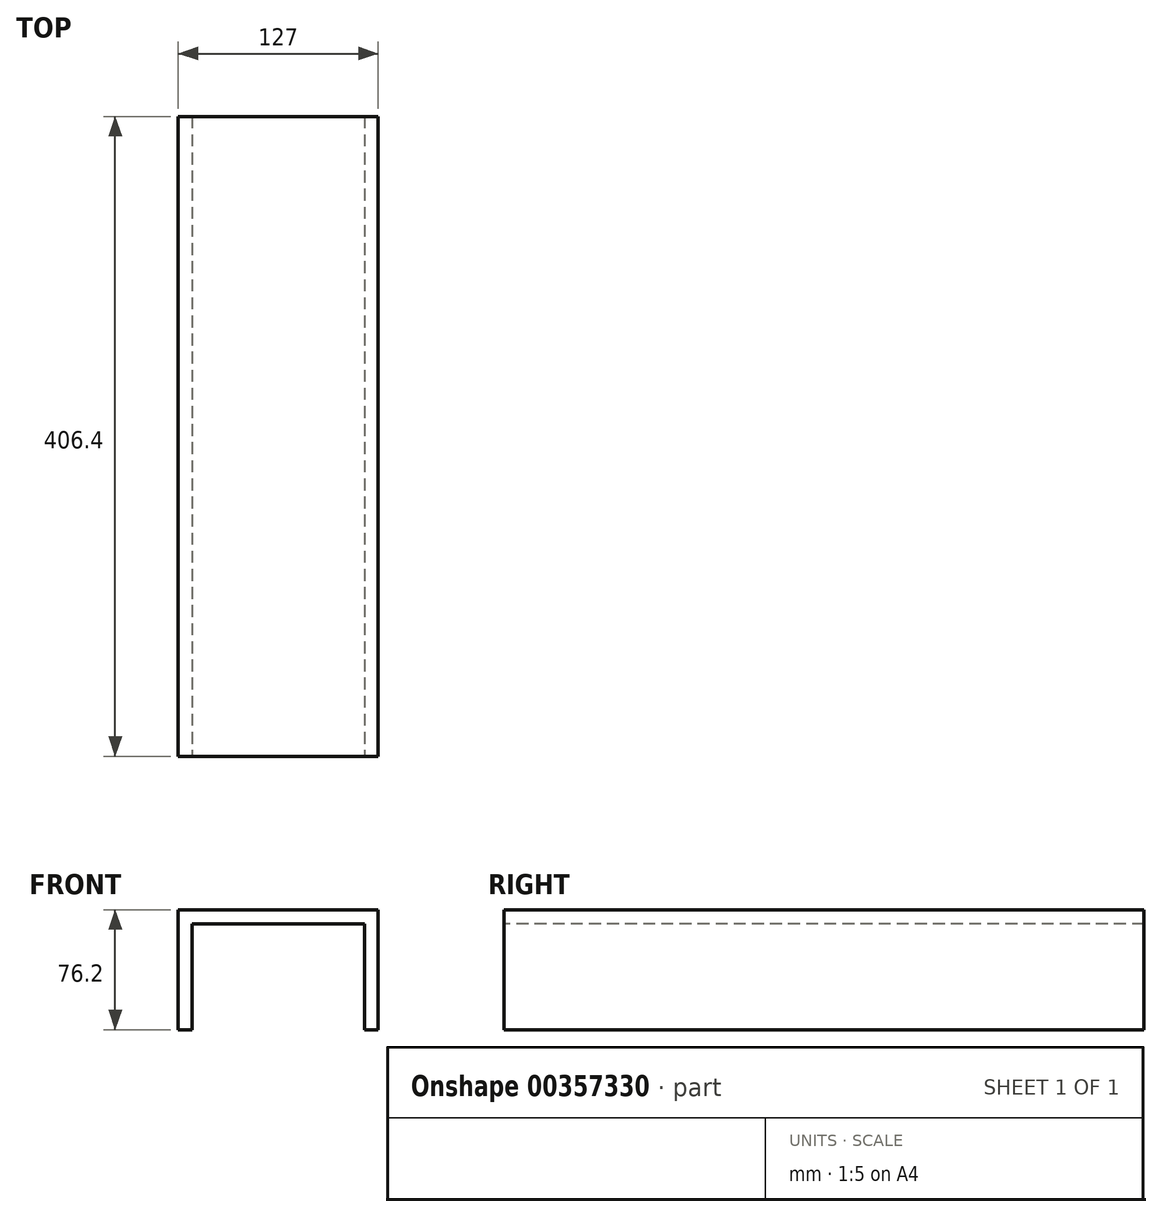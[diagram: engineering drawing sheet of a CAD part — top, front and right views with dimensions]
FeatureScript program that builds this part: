
annotation { "Feature Type Name" : "Feature", "Feature Type Description" : "" }
export const myFeature = defineFeature(function(context is Context, id is Id, definition is map)
    precondition{}
    {
        {
            var Q0;
            Q0=qCreatedBy(makeId("Top.planeOp"),FACE);
            var sketch = newSketch(context, id + "F0", { "sketchPlane" : qUnion([Q0])});
            skLineSegment(sketch, "E0.bottom", {"start": v(-88.1, 201.1) * mm, "end": v(38.9, 201.1) * mm});
            skLineSegment(sketch, "E0.top", {"start": v(-88.1, -205.3) * mm, "end": v(38.9, -205.3) * mm});
            skLineSegment(sketch, "E0.left", {"start": v(-88.1, 201.1) * mm, "end": v(-88.1, -205.3) * mm});
            skLineSegment(sketch, "E0.right", {"start": v(38.9, 201.1) * mm, "end": v(38.9, -205.3) * mm});
            skSolve(sketch);
        }
        {
            var Q0;
            Q0=makeQuery(id+"F0.imprint","IMPRINT",FACE,{"disambiguationData":[TD([[makeQuery(id+"F0.imprint","IMPRINT",EDGE,{"derivedFrom":sQuery(id+"F0.wireOp",EDGE,"E0.bottom")}),-1.0]])]});
            extrude(context, id + "F1", {"entities" : qUnion([Q0]), "depth" : 76.2 * mm});
        }
        {
            var Q0;
            Q0=makeQuery(id+"F1.opExtrude","SWEPT_FACE",FACE,{"disambiguationData":[OSD([sQuery(id+"F0.wireOp",EDGE,"E0.top")])]});
            var sketch = newSketch(context, id + "F2", { "sketchPlane" : qUnion([Q0])});
            skLineSegment(sketch, "E1.bottom", {"start": v(-79.4, 0) * mm, "end": v(-24.6, 0) * mm});
            skLineSegment(sketch, "E1.top", {"start": v(-79.4, 67.3) * mm, "end": v(-24.6, 67.3) * mm});
            skLineSegment(sketch, "E1.left", {"start": v(-79.4, 0) * mm, "end": v(-79.4, 67.3) * mm});
            skLineSegment(sketch, "E2.MirrorCS", {"start": v(30.2, 67.3) * mm, "end": v(-24.6, 67.3) * mm});
            skLineSegment(sketch, "E3.MirrorCS", {"start": v(30.2, 0) * mm, "end": v(30.2, 67.3) * mm});
            skLineSegment(sketch, "E4.MirrorCS", {"start": v(30.2, 0) * mm, "end": v(-24.6, 0) * mm});
            skSolve(sketch);
        }
        {
            var Q0;
            Q0=makeQuery(id+"F2.imprint","IMPRINT",FACE,{"disambiguationData":[TD([[makeQuery(id+"F2.imprint","IMPRINT",EDGE,{"derivedFrom":sQuery(id+"F2.wireOp",EDGE,"E1.bottom")}),1.0]])]});
            extrude(context, id + "F3", {"entities" : qUnion([Q0]), "operationType" : NewBodyOperationType.REMOVE, "oppositeDirection" : true, "depth" : 471.42 * mm});
        }
    });
